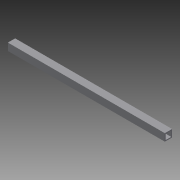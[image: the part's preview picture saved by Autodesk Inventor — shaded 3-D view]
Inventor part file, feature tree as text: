
AUTODESK INVENTOR PART (.ipt)
format: ipt  version: 2015 SP1 (Build 190203100, 203)  size: 90,624 bytes
history: native  units: in
note: dims shown in document units (in); Inventor stores cm internally (conversion verified against a paired STEP export)
features: sketch x2, extrude x1, hole x1, projected_geometry x1
ambient origin geometry x8: Origin, YZ Plane, XZ Plane, XY Plane, X Axis, Y Axis, Z Axis, Center Point
bodies: Solid1 (feature_tree)
feature tree (5):
  extrude  "Extrusion1"  Depth=1.0in
  hole  "Hole1"  [1 undecoded]
  sketch  "Sketch1"  dims[d0=1.0in d1=1.0in]
  sketch  "Sketch2"  dims[d2=0.75in d3=0.75in d4=0.125in d5=0.125in d6=21.5in d7=0.0in d8=0.5in d9=0.5in d10=0.5in d11=0.5in d12=0.25in d13=0.75in d14=0.375in d15=0.25in d16=0.5635in d17=1.0in d18=0.8108in]
  projected_geometry  "Projected Loop1"
note: 1 required parameter value undecoded (feature->parameter linkage not recoverable at this tier; creation-order binding heuristic only, values carry confidence <= 0.55)
